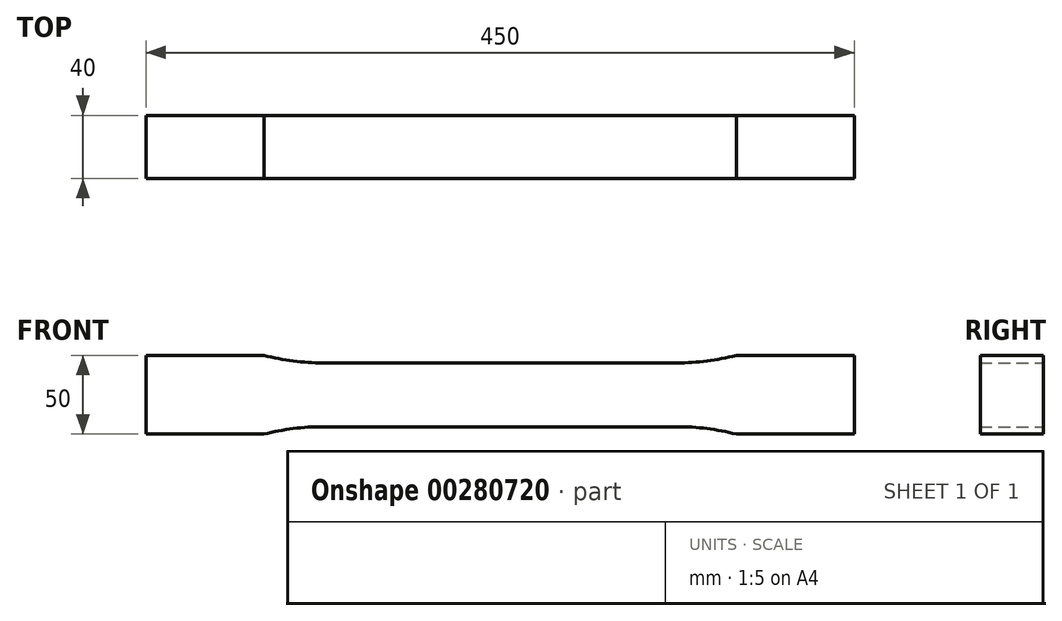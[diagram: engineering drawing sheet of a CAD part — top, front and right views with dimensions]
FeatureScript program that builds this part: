
annotation { "Feature Type Name" : "Feature", "Feature Type Description" : "" }
export const myFeature = defineFeature(function(context is Context, id is Id, definition is map)
    precondition{}
    {
        {
            var Q0;
            Q0=qCreatedBy(makeId("Front.planeOp"),FACE);
            var sketch = newSketch(context, id + "F0", { "sketchPlane" : qUnion([Q0])});
            skLineSegment(sketch, "E0", {"start": v(0, 20.28) * mm, "end": v(112.5, 20.28) * mm});
            skArc(sketch, "E1", {"start": v(112.5, 20.28) * mm, "mid": v(131.4, 21.46) * mm, "end": v(150, 25) * mm});
            skLineSegment(sketch, "E2", {"start": v(150, 25) * mm, "end": v(225, 25) * mm});
            skLineSegment(sketch, "E3", {"start": v(225, 25) * mm, "end": v(225, 0) * mm});
            skLineSegment(sketch, "E4.MirrorCS", {"start": v(0, 20.28) * mm, "end": v(-112.5, 20.28) * mm});
            skLineSegment(sketch, "E5.MirrorCS", {"start": v(-225, 25) * mm, "end": v(-225, 0) * mm});
            skLineSegment(sketch, "E6.MirrorCS", {"start": v(-150, 25) * mm, "end": v(-225, 25) * mm});
            skArc(sketch, "E7.MirrorCS", {"start": v(-112.5, 20.28) * mm, "mid": v(-131.4, 21.46) * mm, "end": v(-150, 25) * mm});
            skArc(sketch, "E8.MirrorCS", {"start": v(-112.5, -20.28) * mm, "mid": v(-131.4, -21.46) * mm, "end": v(-150, -25) * mm});
            skLineSegment(sketch, "E9.MirrorCS", {"start": v(-150, -25) * mm, "end": v(-225, -25) * mm});
            skArc(sketch, "E10.MirrorCS", {"start": v(112.5, -20.28) * mm, "mid": v(131.4, -21.46) * mm, "end": v(150, -25) * mm});
            skLineSegment(sketch, "E11.MirrorCS", {"start": v(150, -25) * mm, "end": v(225, -25) * mm});
            skLineSegment(sketch, "E12.MirrorCS", {"start": v(-225, -25) * mm, "end": v(-225, 0) * mm});
            skLineSegment(sketch, "E13.MirrorCS", {"start": v(0, -20.28) * mm, "end": v(-112.5, -20.28) * mm});
            skLineSegment(sketch, "E14.MirrorCS", {"start": v(225, -25) * mm, "end": v(225, 0) * mm});
            skLineSegment(sketch, "E15.MirrorCS", {"start": v(0, -20.28) * mm, "end": v(112.5, -20.28) * mm});
            skSolve(sketch);
        }
        {
            var Q0;
            Q0 = qSketchRegion(id + "F0", true);
            extrude(context, id + "F1", {"entities" : qUnion([Q0]), "endBound" : BoundingType.SYMMETRIC, "depth" : 40 * mm});
        }
    });
